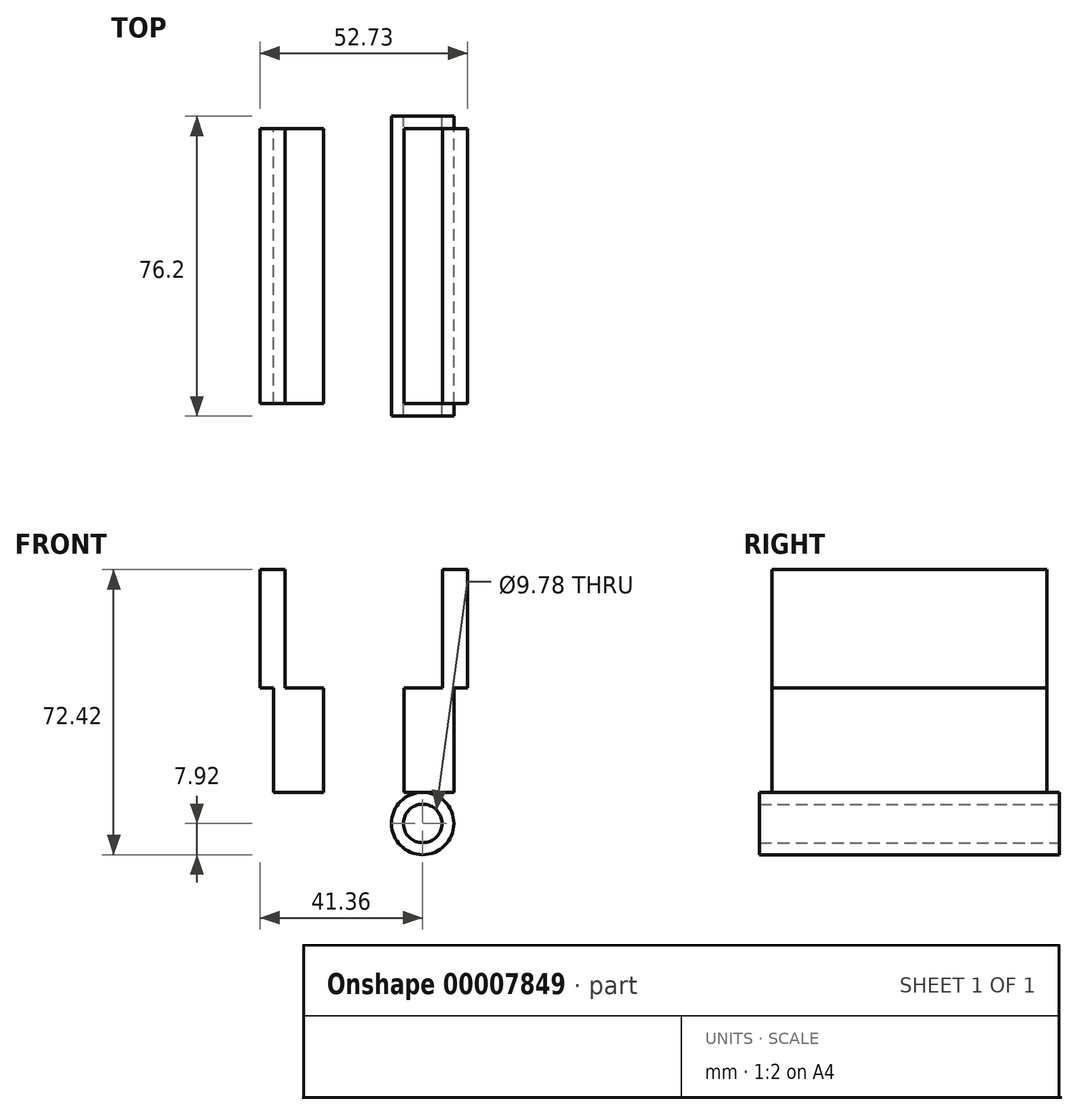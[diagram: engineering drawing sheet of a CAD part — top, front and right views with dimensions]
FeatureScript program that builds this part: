
annotation { "Feature Type Name" : "Feature", "Feature Type Description" : "" }
export const myFeature = defineFeature(function(context is Context, id is Id, definition is map)
    precondition{}
    {
        {
            var Q0;
            Q0=qCreatedBy(makeId("Front.planeOp"),FACE);
            var sketch = newSketch(context, id + "F0", { "sketchPlane" : qUnion([Q0])});
            skCircle(sketch, "E0", {"center": v(0, 0) * mm, "radius": 4.89 * mm});
            skCircle(sketch, "E1", {"center": v(0, 0) * mm, "radius": 7.92 * mm});
            skLineSegment(sketch, "E2.bottom", {"start": v(-4.78, 34.5) * mm, "end": v(7.92, 34.5) * mm});
            skLineSegment(sketch, "E2.top", {"start": v(-4.78, 7.92) * mm, "end": v(7.92, 7.92) * mm});
            skLineSegment(sketch, "E2.left", {"start": v(-4.78, 34.5) * mm, "end": v(-4.78, 7.92) * mm});
            skLineSegment(sketch, "E2.right", {"start": v(7.92, 34.5) * mm, "end": v(7.92, 7.92) * mm});
            skLineSegment(sketch, "E3.bottom", {"start": v(5.02, 64.5) * mm, "end": v(11.37, 64.5) * mm});
            skLineSegment(sketch, "E3.top", {"start": v(5.02, 34.5) * mm, "end": v(11.37, 34.5) * mm});
            skLineSegment(sketch, "E3.left", {"start": v(5.02, 64.5) * mm, "end": v(5.02, 34.5) * mm});
            skLineSegment(sketch, "E3.right", {"start": v(11.37, 64.5) * mm, "end": v(11.37, 34.5) * mm});
            skLineSegment(sketch, "E4", {"start": v(0, 0) * mm, "end": v(-30, 0) * mm, "construction": true});
            skLineSegment(sketch, "E5", {"start": v(-15, 0) * mm, "end": v(-15, 49.5) * mm, "construction": true});
            skLineSegment(sketch, "E6", {"start": v(-35.01, 49.5) * mm, "end": v(5.02, 49.5) * mm, "construction": true});
            skLineSegment(sketch, "E7.MirrorCS", {"start": v(-35.01, 64.5) * mm, "end": v(-35.01, 34.5) * mm});
            skLineSegment(sketch, "E8.MirrorCS", {"start": v(-35.01, 64.5) * mm, "end": v(-41.36, 64.5) * mm});
            skLineSegment(sketch, "E9.MirrorCS", {"start": v(-41.36, 64.5) * mm, "end": v(-41.36, 34.5) * mm});
            skLineSegment(sketch, "E10.MirrorCS", {"start": v(-35.01, 34.5) * mm, "end": v(-41.36, 34.5) * mm});
            skLineSegment(sketch, "E11.MirrorCS", {"start": v(-25.22, 34.5) * mm, "end": v(-37.92, 34.5) * mm});
            skLineSegment(sketch, "E12.MirrorCS", {"start": v(-25.22, 34.5) * mm, "end": v(-25.22, 7.92) * mm});
            skLineSegment(sketch, "E13.MirrorCS", {"start": v(-37.92, 34.5) * mm, "end": v(-37.92, 7.92) * mm});
            skLineSegment(sketch, "E14.MirrorCS", {"start": v(-25.22, 7.92) * mm, "end": v(-37.92, 7.92) * mm});
            skCircle(sketch, "E15.MirrorC", {"center": v(-30, 0) * mm, "radius": 7.92 * mm});
            skCircle(sketch, "E16.MirrorC", {"center": v(-30, 0) * mm, "radius": 4.89 * mm});
            skSolve(sketch);
        }
        {
            var Q0;
            Q0=makeQuery(id+"F0.imprint","IMPRINT",FACE,{"disambiguationData":[TD([[makeQuery(id+"F0.imprint","IMPRINT",EDGE,{"derivedFrom":sQuery(id+"F0.wireOp",EDGE,"E0")}),-1.0]])]});
            var Q1;
            Q1=makeQuery(id+"F0.imprint","IMPRINT",FACE,{"disambiguationData":[TD([[makeQuery(id+"F0.imprint","IMPRINT",EDGE,{"derivedFrom":sQuery(id+"F0.wireOp",EDGE,"E15.MirrorC")}),-1.0]])]});
            extrude(context, id + "F1", {"entities" : qUnion([Q0, Q1]), "endBound" : BoundingType.SYMMETRIC, "depth" : 76.2 * mm});
        }
        {
            var Q0;
            {var subQ2=sQuery(id+"F0.wireOp",EDGE,"E2.bottom");Q0=makeQuery(id+"F0.imprint","IMPRINT",FACE,{"disambiguationData":[TD([[makeQuery(id+"F0.imprint","IMPRINT",EDGE,{"derivedFrom":subQ2}),-1.0]])]});}
            var Q1;
            {var subQ3=sQuery(id+"F0.wireOp",EDGE,"E12.MirrorCS");Q1=makeQuery(id+"F0.imprint","IMPRINT",FACE,{"disambiguationData":[TD([[makeQuery(id+"F0.imprint","IMPRINT",EDGE,{"derivedFrom":subQ3}),-1.0]])]});}
            var Q2;
            {var subQ2=sQuery(id+"F0.wireOp",EDGE,"E7.MirrorCS");Q2=makeQuery(id+"F0.imprint","IMPRINT",FACE,{"disambiguationData":[TD([[makeQuery(id+"F0.imprint","IMPRINT",EDGE,{"derivedFrom":subQ2}),-1.0]])]});}
            var Q3;
            Q3=makeQuery(id+"F0.imprint","IMPRINT",FACE,{"disambiguationData":[TD([[makeQuery(id+"F0.imprint","IMPRINT",EDGE,{"derivedFrom":sQuery(id+"F0.wireOp",EDGE,"E3.bottom")}),-1.0]])]});
            extrude(context, id + "F2", {"entities" : qUnion([Q0, Q1, Q2, Q3]), "endBound" : BoundingType.SYMMETRIC, "depth" : 69.85 * mm});
        }
    });
